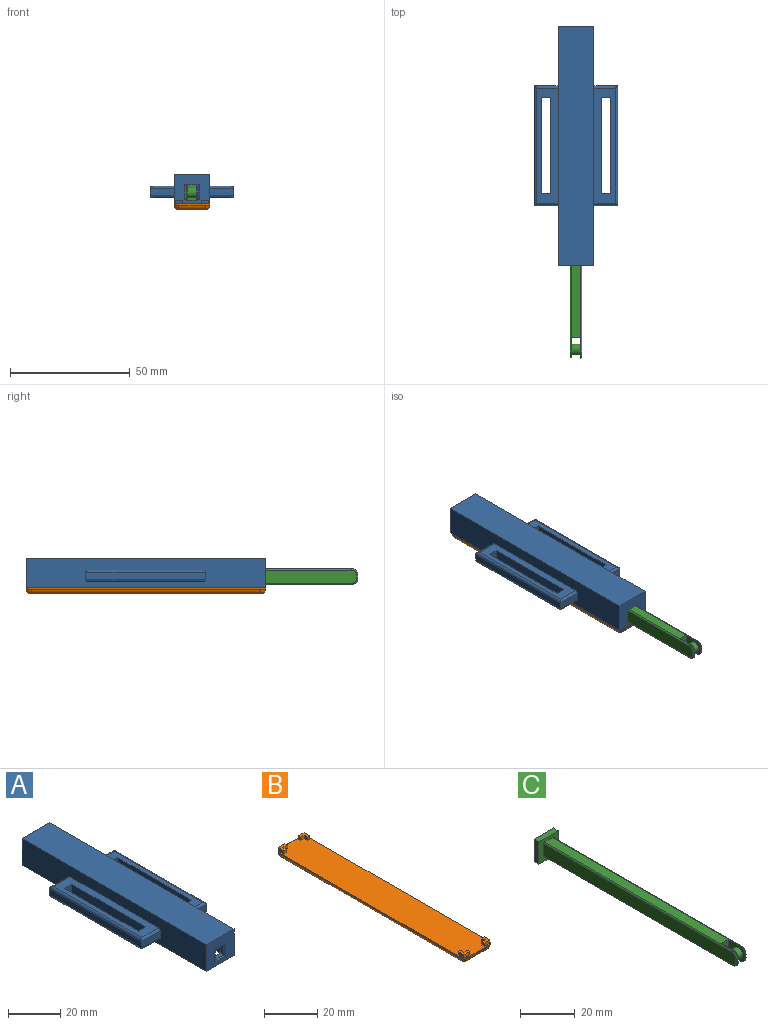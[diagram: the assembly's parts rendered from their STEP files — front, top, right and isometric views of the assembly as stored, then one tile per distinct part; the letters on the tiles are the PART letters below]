
ASSEMBLY  parts=3 mates=2
PART A: 77 faces, bbox 35x100x12.5 mm
  f0: plane 100x12.5mm, normal (-1,0,0), area 1000.9mm2, adj f2,f4,f5,f6,f62,f63,f64,f65
  f1: plane 100x12.5mm, normal (1,0,0), area 1000.9mm2, adj f2,f4,f5,f6,f47,f48,f49,f50
  f2: plane 100x15mm, normal (0,0,-1), area 525mm2, adj f0,f1,f3,f4,f5,f7,f8,f9
  f3: plane 10x10mm, normal (0,1,0), area 75mm2, adj f2,f7,f9,f10,f11,f12,f13,f14
  f4: plane 15x12.5mm, normal (0,1,0), area 187.5mm2, adj f0,f1,f2,f6
  f5: plane 15x12.5mm, normal (0,-1,0), area 151.5mm2, adj f0,f1,f2,f6,f43,f44,f45,f46
  f6: plane 100x15mm, normal (0,0,1), area 1500mm2, adj f0,f1,f4,f5
  f7: plane 95x10mm, normal (-1,0,0), area 950mm2, adj f2,f3,f8,f10
  f8: plane 10x10mm, normal (0,-1,0), area 100mm2, adj f2,f7,f9,f10
  f9: plane 95x10mm, normal (1,0,0), area 950mm2, adj f2,f3,f8,f10
  f10: plane 95x10mm, normal (0,0,-1), area 950mm2, adj f3,f7,f8,f9
  f11: plane 5x2mm, normal (1,0,0), area 10mm2, adj f3,f13,f14,f44
  f12: plane 5x2mm, normal (-1,0,0), area 10mm2, adj f3,f13,f14,f45
  f13: plane 5x2mm, normal (0,0,-1), area 10mm2, adj f3,f11,f12,f43
  f14: plane 5x2mm, normal (0,0,1), area 10mm2, adj f3,f11,f12,f46
  f15: plane 1.75x1.5mm, normal (-1,0,0), area 2.6mm2, adj f2,f16,f20,f21
  f16: plane 1.75x1.5mm, normal (0,-1,0), area 2.6mm2, adj f2,f15,f17,f21
  f17: plane 1.5x1.25mm, normal (-1,0,0), area 1.9mm2, adj f2,f16,f18,f21
  f18: plane 3x1.5mm, normal (0,1,0), area 4.5mm2, adj f2,f17,f19,f21
  f19: plane 3x1.5mm, normal (1,0,0), area 4.5mm2, adj f2,f18,f20,f21
  f20: plane 1.5x1.25mm, normal (0,-1,0), area 1.9mm2, adj f2,f15,f19,f21
  f21: plane 3x3mm, normal (0,0,-1), area 5.9mm2, adj f15,f16,f17,f18,f19,f20
  f22: plane 1.75x1.5mm, normal (0,-1,0), area 2.6mm2, adj f2,f23,f27,f28
  f23: plane 1.75x1.5mm, normal (1,0,0), area 2.6mm2, adj f2,f22,f24,f28
  f24: plane 1.5x1.25mm, normal (0,-1,0), area 1.9mm2, adj f2,f23,f25,f28
  f25: plane 3x1.5mm, normal (-1,0,0), area 4.5mm2, adj f2,f24,f26,f28
  f26: plane 3x1.5mm, normal (0,1,0), area 4.5mm2, adj f2,f25,f27,f28
  f27: plane 1.5x1.25mm, normal (1,0,0), area 1.9mm2, adj f2,f22,f26,f28
  f28: plane 3x3mm, normal (0,0,-1), area 5.9mm2, adj f22,f23,f24,f25,f26,f27
  f29: plane 3x1.5mm, normal (-1,0,0), area 4.5mm2, adj f2,f30,f34,f35
  f30: plane 1.5x1.25mm, normal (0,1,0), area 1.9mm2, adj f2,f29,f31,f35
  f31: plane 1.75x1.5mm, normal (1,0,0), area 2.6mm2, adj f2,f30,f32,f35
  f32: plane 1.75x1.5mm, normal (0,1,0), area 2.6mm2, adj f2,f31,f33,f35
  f33: plane 1.5x1.25mm, normal (1,0,0), area 1.9mm2, adj f2,f32,f34,f35
  f34: plane 3x1.5mm, normal (0,-1,0), area 4.5mm2, adj f2,f29,f33,f35
  f35: plane 3x3mm, normal (0,0,-1), area 5.9mm2, adj f29,f30,f31,f32,f33,f34
  f36: plane 3.3x1.5mm, normal (1,0,0), area 5mm2, adj f2,f37,f41,f42
  f37: plane 3.3x1.5mm, normal (0,-1,0), area 5mm2, adj f2,f36,f38,f42
  f38: plane 1.5x1.25mm, normal (-1,0,0), area 1.9mm2, adj f2,f37,f39,f42
  f39: plane 1.8x1.5mm, normal (0,1,0), area 2.7mm2, adj f2,f38,f40,f42
  f40: plane 2.05x1.5mm, normal (-1,0,0), area 3.1mm2, adj f2,f39,f41,f42
  f41: plane 1.5x1.5mm, normal (0,1,0), area 2.3mm2, adj f2,f36,f40,f42
  f42: plane 3.3x3.3mm, normal (0,0,-1), area 7.2mm2, adj f36,f37,f38,f39,f40,f41
  f43: cylinder r=0.5mm len=6mm, axis (1,0,0), area 4.2mm2, adj f5,f13,f44,f45
  f44: cylinder r=0.5mm len=6mm, axis (0,0,-1), area 4.2mm2, adj f5,f11,f43,f46
  f45: cylinder r=0.5mm len=6mm, axis (0,0,1), area 4.2mm2, adj f5,f12,f43,f46
  f46: cylinder r=0.5mm len=6mm, axis (1,0,0), area 4.2mm2, adj f5,f14,f44,f45
  f47: plane 48x9mm, normal (0,0,1), area 272mm2, adj f1,f52,f53,f54,f55,f56,f57,f58
  f48: plane 48x9mm, normal (0,0,-1), area 272mm2, adj f1,f52,f53,f54,f55,f59,f60,f61
  f49: plane 10x3mm, normal (0,1,0), area 30mm2, adj f1,f51,f58,f59
  f50: plane 10x3mm, normal (0,-1,0), area 30mm2, adj f1,f51,f56,f61
  f51: plane 50x3mm, normal (1,0,0), area 150mm2, adj f49,f50,f57,f60
  f52: plane 40x5mm, normal (-1,0,0), area 200mm2, adj f47,f48,f53,f55
  f53: plane 5x4mm, normal (0,-1,0), area 20mm2, adj f47,f48,f52,f54
  f54: plane 40x5mm, normal (1,0,0), area 200mm2, adj f47,f48,f53,f55
  f55: plane 5x4mm, normal (0,1,0), area 20mm2, adj f47,f48,f52,f54
  f56: cylinder r=1mm len=10mm, axis (-1,0,0), area 15.1mm2, adj f1,f47,f50,f57
  f57: cylinder r=1mm len=50mm, axis (0,1,0), area 77.4mm2, adj f47,f51,f56,f58
  f58: cylinder r=1mm len=10mm, axis (1,0,0), area 15.1mm2, adj f1,f47,f49,f57
  f59: cylinder r=1mm len=10mm, axis (-1,0,0), area 15.1mm2, adj f1,f48,f49,f60
  f60: cylinder r=1mm len=50mm, axis (0,-1,0), area 77.4mm2, adj f48,f51,f59,f61
  f61: cylinder r=1mm len=10mm, axis (1,0,0), area 15.1mm2, adj f1,f48,f50,f60
  f62: plane 48x9mm, normal (0,0,1), area 272mm2, adj f0,f67,f68,f69,f70,f71,f72,f73
  f63: plane 48x9mm, normal (0,0,-1), area 272mm2, adj f0,f67,f68,f69,f70,f74,f75,f76
  f64: plane 10x3mm, normal (0,1,0), area 30mm2, adj f0,f66,f73,f74
  f65: plane 10x3mm, normal (0,-1,0), area 30mm2, adj f0,f66,f71,f76
  f66: plane 50x3mm, normal (-1,0,0), area 150mm2, adj f64,f65,f72,f75
  f67: plane 40x5mm, normal (1,0,0), area 200mm2, adj f62,f63,f68,f70
  f68: plane 5x4mm, normal (0,-1,0), area 20mm2, adj f62,f63,f67,f69
  f69: plane 40x5mm, normal (-1,0,0), area 200mm2, adj f62,f63,f68,f70
  f70: plane 5x4mm, normal (0,1,0), area 20mm2, adj f62,f63,f67,f69
  f71: cylinder r=1mm len=10mm, axis (1,0,0), area 15.1mm2, adj f0,f62,f65,f72
  f72: cylinder r=1mm len=50mm, axis (0,1,0), area 77.4mm2, adj f62,f66,f71,f73
  f73: cylinder r=1mm len=10mm, axis (-1,0,0), area 15.1mm2, adj f0,f62,f64,f72
  f74: cylinder r=1mm len=10mm, axis (1,0,0), area 15.1mm2, adj f0,f63,f64,f75
  f75: cylinder r=1mm len=50mm, axis (0,-1,0), area 77.4mm2, adj f63,f66,f74,f76
  f76: cylinder r=1mm len=10mm, axis (-1,0,0), area 15.1mm2, adj f0,f63,f65,f75
PART B: 46 faces, bbox 15x100x4 mm
  f0: plane 100x15mm, normal (0,0,1), area 1472mm2, adj f1,f2,f3,f4,f6,f7,f8,f9
  f1: plane 11x0.5mm, normal (0,1,0), area 5.5mm2, adj f0,f39,f43,f45
  f2: plane 96x0.5mm, normal (-1,0,0), area 48mm2, adj f0,f36,f42,f45
  f3: plane 11x0.5mm, normal (0,-1,0), area 5.5mm2, adj f0,f34,f36,f37
  f4: plane 96x0.5mm, normal (1,0,0), area 48mm2, adj f0,f34,f38,f39
  f5: plane 96x11mm, normal (0,0,-1), area 1056mm2, adj f37,f38,f42,f43
  f6: plane 3.63x1.5mm, normal (0,1,0), area 5.4mm2, adj f0,f7,f11,f12
  f7: plane 3x1.5mm, normal (-1,0,0), area 4.5mm2, adj f0,f6,f8,f12
  f8: plane 1.5x1.25mm, normal (0,-1,0), area 1.9mm2, adj f0,f7,f9,f12
  f9: plane 1.75x1.5mm, normal (1,0,0), area 2.6mm2, adj f0,f8,f10,f12
  f10: plane 2.38x1.5mm, normal (0,-1,0), area 3.6mm2, adj f0,f9,f11,f12
  f11: plane 1.5x1.25mm, normal (1,0,0), area 1.9mm2, adj f0,f6,f10,f12
  f12: plane 3.63x3mm, normal (0,0,1), area 6.7mm2, adj f6,f7,f8,f9,f10,f11
  f13: plane 1.75x1.5mm, normal (0,-1,0), area 2.6mm2, adj f0,f14,f18,f19
  f14: plane 1.75x1.5mm, normal (-1,0,0), area 2.6mm2, adj f0,f13,f15,f19
  f15: plane 1.5x1.25mm, normal (0,-1,0), area 1.9mm2, adj f0,f14,f16,f19
  f16: plane 3x1.5mm, normal (1,0,0), area 4.5mm2, adj f0,f15,f17,f19
  f17: plane 3x1.5mm, normal (0,1,0), area 4.5mm2, adj f0,f16,f18,f19
  f18: plane 1.5x1.25mm, normal (-1,0,0), area 1.9mm2, adj f0,f13,f17,f19
  f19: plane 3x3mm, normal (0,0,1), area 5.9mm2, adj f13,f14,f15,f16,f17,f18
  f20: plane 3x1.5mm, normal (0,-1,0), area 4.5mm2, adj f0,f21,f25,f26
  f21: plane 3x1.5mm, normal (1,0,0), area 4.5mm2, adj f0,f20,f22,f26
  f22: plane 1.5x1.25mm, normal (0,1,0), area 1.9mm2, adj f0,f21,f23,f26
  f23: plane 1.75x1.5mm, normal (-1,0,0), area 2.6mm2, adj f0,f22,f24,f26
  f24: plane 1.75x1.5mm, normal (0,1,0), area 2.6mm2, adj f0,f23,f25,f26
  f25: plane 1.5x1.25mm, normal (-1,0,0), area 1.9mm2, adj f0,f20,f24,f26
  f26: plane 3x3mm, normal (0,0,1), area 5.9mm2, adj f20,f21,f22,f23,f24,f25
  f27: plane 1.75x1.5mm, normal (0,1,0), area 2.6mm2, adj f0,f28,f32,f33
  f28: plane 1.75x1.5mm, normal (1,0,0), area 2.6mm2, adj f0,f27,f29,f33
  f29: plane 1.5x1.25mm, normal (0,1,0), area 1.9mm2, adj f0,f28,f30,f33
  f30: plane 3x1.5mm, normal (-1,0,0), area 4.5mm2, adj f0,f29,f31,f33
  f31: plane 3x1.5mm, normal (0,-1,0), area 4.5mm2, adj f0,f30,f32,f33
  f32: plane 1.5x1.25mm, normal (1,0,0), area 1.9mm2, adj f0,f27,f31,f33
  f33: plane 3x3mm, normal (0,0,1), area 5.9mm2, adj f27,f28,f29,f30,f31,f32
  f34: cylinder r=2mm len=2mm, axis (0,0,1), area 1.6mm2, adj f0,f3,f4,f35
  f35: sphere r=2mm, area 6.3mm2, adj f34,f37,f38
  f36: cylinder r=2mm len=2mm, axis (0,0,-1), area 1.6mm2, adj f0,f2,f3,f40
  f37: cylinder r=2mm len=11mm, axis (1,0,0), area 34.6mm2, adj f3,f5,f35,f40
  f38: cylinder r=2mm len=96mm, axis (0,1,0), area 301.6mm2, adj f4,f5,f35,f41
  f39: cylinder r=2mm len=2mm, axis (0,0,-1), area 1.6mm2, adj f0,f1,f4,f41
  f40: sphere r=2mm, area 6.3mm2, adj f36,f37,f42
  f41: sphere r=2mm, area 6.3mm2, adj f38,f39,f43
  f42: cylinder r=2mm len=96mm, axis (0,-1,0), area 301.6mm2, adj f2,f5,f40,f44
  f43: cylinder r=2mm len=11mm, axis (-1,0,0), area 34.6mm2, adj f1,f5,f41,f44
  f44: sphere r=2mm, area 6.3mm2, adj f42,f43,f45
  f45: cylinder r=2mm len=2mm, axis (0,0,1), area 1.6mm2, adj f0,f1,f2,f44
PART C: 30 faces, bbox 10x102.2x10 mm
  f0: plane 10x10mm, normal (0,-1,0), area 67.7mm2, adj f1,f3,f4,f5,f8,f9,f13,f14
  f1: plane 10x2.5mm, normal (1,0,0), area 25mm2, adj f0,f2,f4,f5
  f2: plane 10x10mm, normal (0,1,0), area 100mm2, adj f1,f3,f4,f5
  f3: plane 10x2.5mm, normal (-1,0,0), area 25mm2, adj f0,f2,f4,f5
  f4: plane 10x2.5mm, normal (0,0,1), area 25mm2, adj f0,f1,f2,f3
  f5: plane 10x2.5mm, normal (0,0,-1), area 25mm2, adj f0,f1,f2,f3
  f6: plane 8.75x6.5mm, normal (-1,0,0), area 38.3mm2, adj f7,f12,f13,f14,f15,f17,f19
  f7: plane 1.5x0.25mm, normal (0,-1,0), area 0.4mm2, adj f6,f17,f19,f27
  f8: plane 99x5.5mm, normal (1,0,0), area 542.8mm2, adj f0,f25,f26,f27,f28,f29
  f9: plane 99x5.5mm, normal (-1,0,0), area 542.8mm2, adj f0,f20,f21,f22,f23,f24
  f10: plane 1.5x0.25mm, normal (0,-1,0), area 0.4mm2, adj f11,f16,f18,f22
  f11: plane 8.75x6.5mm, normal (1,0,0), area 38.3mm2, adj f10,f12,f13,f14,f15,f16,f18
  f12: plane 6.5x3.5mm, normal (0,-1,0), area 22.8mm2, adj f6,f11,f13,f14
  f13: plane 97x4mm, normal (0,0,1), area 366.1mm2, adj f0,f6,f11,f12,f18,f19,f20,f25
  f14: plane 97x4mm, normal (0,0,-1), area 366.1mm2, adj f0,f6,f11,f12,f16,f17,f24,f29
  f15: cylinder r=2.25mm len=4.5mm, axis (1,0,0), area 49.5mm2, adj f6,f11
  f16: cylinder r=2.5mm len=2.5mm, axis (1,0,0), area 1mm2, adj f10,f11,f14,f23
  f17: cylinder r=2.5mm len=2.5mm, axis (1,0,0), area 1mm2, adj f6,f7,f14,f28
  f18: cylinder r=2.5mm len=2.5mm, axis (-1,0,0), area 1mm2, adj f10,f11,f13,f21
  f19: cylinder r=2.5mm len=2.5mm, axis (-1,0,0), area 1mm2, adj f6,f7,f13,f26
  f20: cylinder r=0.5mm len=97mm, axis (0,1,0), area 76.2mm2, adj f0,f9,f13,f21
  f21: torus R=2mm, axis (1,0,0), area 2.9mm2, adj f9,f18,f20,f22
  f22: cylinder r=0.5mm len=1.5mm, axis (0,0,-1), area 1.2mm2, adj f9,f10,f21,f23
  f23: torus R=2mm, axis (1,0,0), area 2.9mm2, adj f9,f16,f22,f24
  f24: cylinder r=0.5mm len=97mm, axis (0,-1,0), area 76.2mm2, adj f0,f9,f14,f23
  f25: cylinder r=0.5mm len=97mm, axis (0,-1,0), area 76.2mm2, adj f0,f8,f13,f26
  f26: torus R=2mm, axis (1,0,0), area 2.9mm2, adj f8,f19,f25,f27
  f27: cylinder r=0.5mm len=1.5mm, axis (0,0,1), area 1.2mm2, adj f7,f8,f26,f28
  f28: torus R=2mm, axis (1,0,0), area 2.9mm2, adj f8,f17,f27,f29
  f29: cylinder r=0.5mm len=97mm, axis (0,1,0), area 76.2mm2, adj f0,f8,f14,f28
PLACE A rot(axis=(0,1,0),0deg) t=(-17.17,7.85,15.06)mm fixed
PLACE B rot(axis=(0,1,0),0deg) t=(-17.16,7.76,7.56)mm
PLACE C rot(axis=(0,-1,0),180deg) t=(-17.17,-29.86,15.06)mm
MATE slider C.f2 <-> A.f8  axis (0,1,0) through (-17.17,21.14,15.06)mm
MATE fastened A.f2 <-> B.f0  axis (0,0,-1) through (-17.15,7.73,10.06)mm
